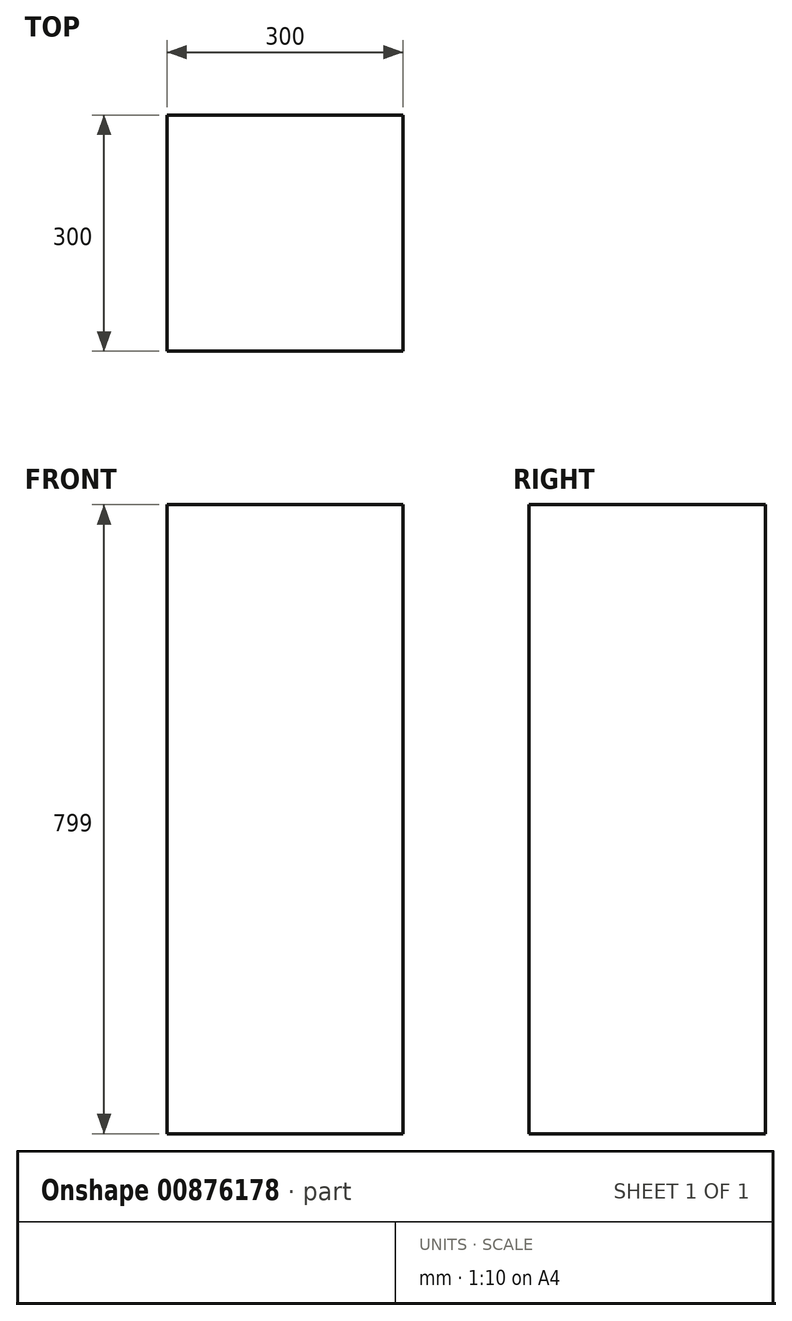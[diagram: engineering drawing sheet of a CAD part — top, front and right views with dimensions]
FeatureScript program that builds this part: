
annotation { "Feature Type Name" : "Feature", "Feature Type Description" : "" }
export const myFeature = defineFeature(function(context is Context, id is Id, definition is map)
    precondition{}
    {
        {
            var Q0;
            Q0=qCreatedBy(makeId("Top.planeOp"),FACE);
            var sketch = newSketch(context, id + "F0", { "sketchPlane" : qUnion([Q0])});
            skLineSegment(sketch, "E0.bottom", {"start": v(150, -150) * mm, "end": v(-150, -150) * mm});
            skLineSegment(sketch, "E0.top", {"start": v(150, 150) * mm, "end": v(-150, 150) * mm});
            skLineSegment(sketch, "E0.left", {"start": v(150, -150) * mm, "end": v(150, 150) * mm});
            skLineSegment(sketch, "E0.right", {"start": v(-150, -150) * mm, "end": v(-150, 150) * mm});
            skPoint(sketch, "E0.middle", {"position": v(0, 0) * mm});
            skSolve(sketch);
        }
        {
            var Q0;
            Q0=makeQuery(id+"F0.imprint","IMPRINT",FACE,{"disambiguationData":[TD([[makeQuery(id+"F0.imprint","IMPRINT",EDGE,{"derivedFrom":sQuery(id+"F0.wireOp",EDGE,"E0.bottom")}),-1.0]])]});
            extrude(context, id + "F1", {"entities" : qUnion([Q0]), "depth" : 799 * mm, "offsetDistance" : 25 * mm});
        }
    });
